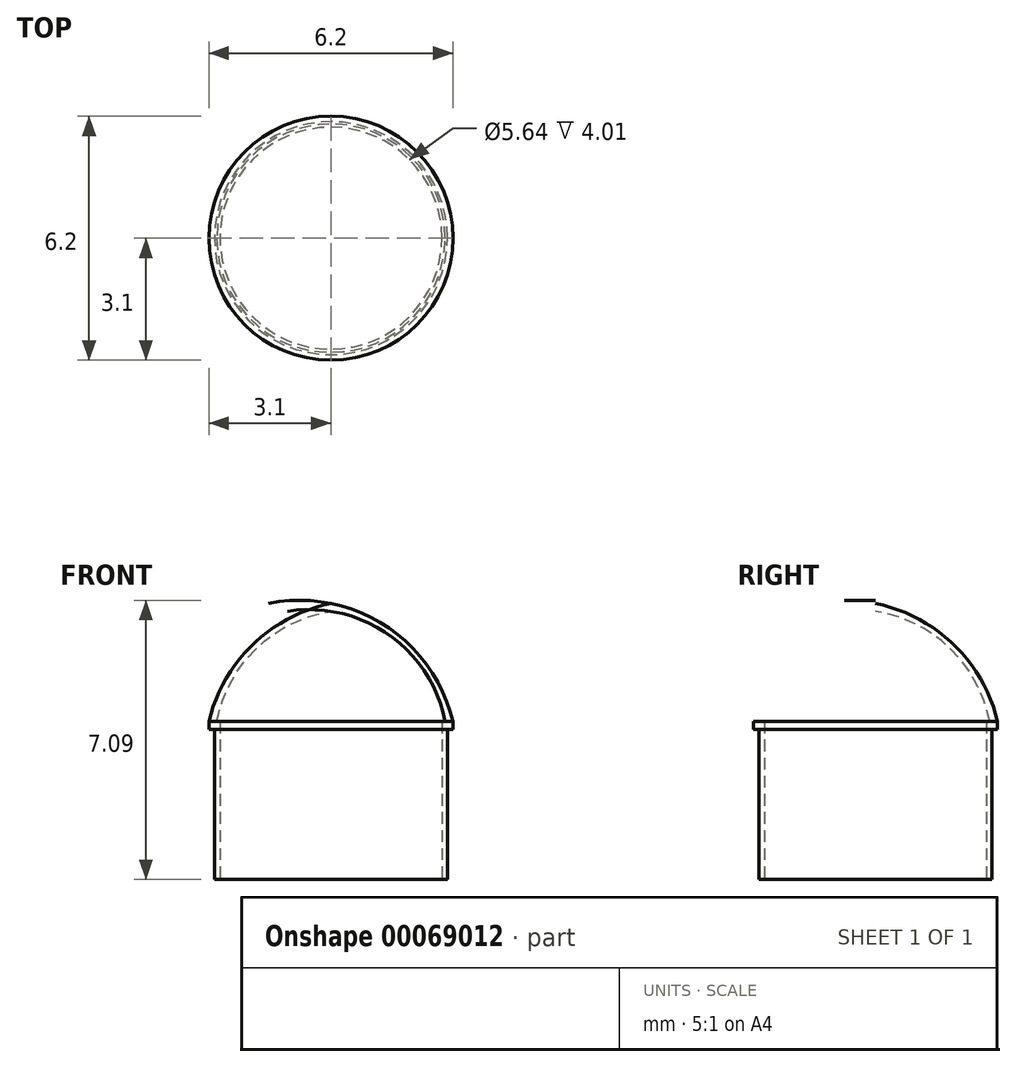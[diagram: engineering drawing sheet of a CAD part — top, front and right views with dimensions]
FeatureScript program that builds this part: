
annotation { "Feature Type Name" : "Feature", "Feature Type Description" : "" }
export const myFeature = defineFeature(function(context is Context, id is Id, definition is map)
    precondition{}
    {
        {
            var Q0;
            Q0=qCreatedBy(makeId("Top.planeOp"),FACE);
            var sketch = newSketch(context, id + "F0", { "sketchPlane" : qUnion([Q0])});
            skCircle(sketch, "E0", {"center": v(0, 0) * mm, "radius": 2.96 * mm});
            skCircle(sketch, "E1", {"center": v(0, 0) * mm, "radius": 2.82 * mm});
            skSolve(sketch);
        }
        {
            var Q0;
            Q0 = qSketchRegion(id + "F0", true);
            extrude(context, id + "F1", {"entities" : qUnion([Q0]), "depth" : 3.8 * mm});
        }
        {
            var Q0;
            Q0=makeQuery(id+"F1.opExtrude","CAP_FACE",FACE,{"disambiguationData":[OSD([sQuery(id+"F0.wireOp",EDGE,"E0"),sQuery(id+"F0.wireOp",EDGE,"E1")])],"isStart":false});
            var sketch = newSketch(context, id + "F2", { "sketchPlane" : qUnion([Q0])});
            skCircle(sketch, "E2", {"center": v(0, 0) * mm, "radius": 3.1 * mm});
            skSolve(sketch);
        }
        {
            var Q0;
            Q0=makeQuery(id+"F2.imprint","IMPRINT",FACE,{"disambiguationData":[TD([[makeQuery(id+"F2.imprint","IMPRINT",EDGE,{"derivedFrom":sQuery(id+"F2.wireOp",EDGE,"E2")}),1.0]])]});
            var Q1;
            Q1=makeQuery(id+"F2.imprint","IMPRINT",FACE,{"disambiguationData":[TD([[makeQuery(id+"F2.imprint","IMPRINT",EDGE,{"derivedFrom":makeQuery(id+"F1.opExtrude","CAP_EDGE",EDGE,{"disambiguationData":[OSD([sQuery(id+"F0.wireOp",EDGE,"E0")])],"isStart":false})}),1.0]])]});
            extrude(context, id + "F3", {"entities" : qUnion([Q0, Q1]), "operationType" : NewBodyOperationType.ADD, "depth" : .2 * mm});
        }
        {
            var Q0;
            Q0=qCreatedBy(makeId("Right.planeOp"),FACE);
            var sketch = newSketch(context, id + "F4", { "sketchPlane" : qUnion([Q0])});
            skPoint(sketch, "E3", {"position": v(0, 0) * mm});
            skPoint(sketch, "E4", {"position": v(0, 4) * mm});
            skPoint(sketch, "E5", {"position": v(-3.1, 4) * mm});
            skPoint(sketch, "E6", {"position": v(0, 7) * mm});
            skArc(sketch, "E7", {"start": v(0, 7) * mm, "mid": v(-1.99, 5.96) * mm, "end": v(-3.1, 4.01) * mm});
            skArc(sketch, "E8", {"start": v(0, 6.81) * mm, "mid": v(-1.9, 5.87) * mm, "end": v(-2.9, 4) * mm});
            skLineSegment(sketch, "E9", {"start": v(0, 7) * mm, "end": v(0, 6.81) * mm});
            skLineSegment(sketch, "E10", {"start": v(-2.9, 4) * mm, "end": v(-3.1, 4) * mm});
            skLineSegment(sketch, "E11", {"start": v(0, 4) * mm, "end": v(0, 7.71) * mm, "construction": true});
            skSolve(sketch);
        }
        {
            var Q0;
            Q0=makeQuery(id+"F4.imprint","IMPRINT",FACE,{"disambiguationData":[TD([[makeQuery(id+"F4.imprint","IMPRINT",EDGE,{"derivedFrom":sQuery(id+"F4.wireOp",EDGE,"E7")}),1.0]])]});
            var Q1;
            Q1=sQuery(id+"F4.wireOp",EDGE,"E11");
            revolve(context, id + "F5", {"operationType" : NewBodyOperationType.ADD, "entities" : qUnion([Q0]), "axis" : qUnion([Q1]), "revolveType" : RevolveType.FULL});
        }
    });
